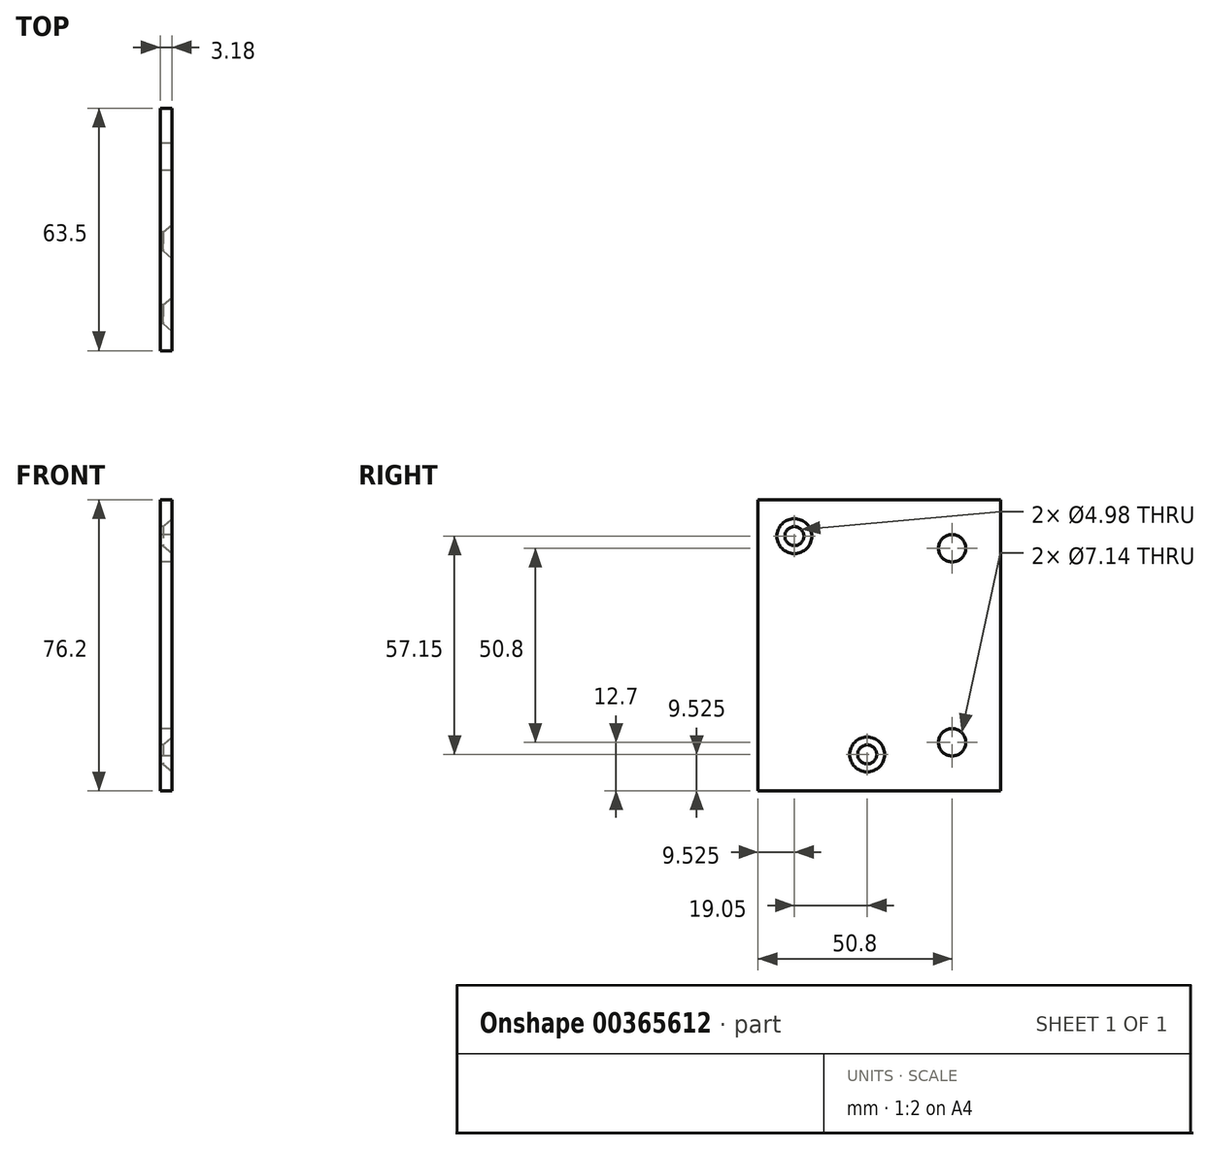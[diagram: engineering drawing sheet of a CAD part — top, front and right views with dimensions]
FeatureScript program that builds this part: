
annotation { "Feature Type Name" : "Feature", "Feature Type Description" : "" }
export const myFeature = defineFeature(function(context is Context, id is Id, definition is map)
    precondition{}
    {
        {
            var Q0;
            Q0=qCreatedBy(makeId("Right.planeOp"),FACE);
            var sketch = newSketch(context, id + "F0", { "sketchPlane" : qUnion([Q0])});
            skLineSegment(sketch, "E0.bottom", {"start": v(31.75, -38.1) * mm, "end": v(-31.75, -38.1) * mm});
            skLineSegment(sketch, "E0.top", {"start": v(31.75, 38.1) * mm, "end": v(-31.75, 38.1) * mm});
            skLineSegment(sketch, "E0.left", {"start": v(31.75, -38.1) * mm, "end": v(31.75, 38.1) * mm});
            skLineSegment(sketch, "E0.right", {"start": v(-31.75, -38.1) * mm, "end": v(-31.75, 38.1) * mm});
            skPoint(sketch, "E0.middle", {"position": v(0, 0) * mm});
            skSolve(sketch);
        }
        {
            var Q0;
            Q0=qSketchRegion(id+"F0",true);
            extrude(context, id + "F1", {"entities" : qUnion([Q0]), "depth" : 3.17 * mm, "offsetDistance" : 25.4 * mm});
        }
        {
            var Q0;
            Q0=makeQuery(id+"F1.opExtrude","CAP_FACE",FACE,{"disambiguationData":[OSD([sQuery(id+"F0.wireOp",EDGE,"E0.bottom"),sQuery(id+"F0.wireOp",EDGE,"E0.top"),sQuery(id+"F0.wireOp",EDGE,"E0.left"),sQuery(id+"F0.wireOp",EDGE,"E0.right")])],"isStart":false});
            var sketch = newSketch(context, id + "F2", { "sketchPlane" : qUnion([Q0])});
            skPoint(sketch, "E1", {"position": v(-22.23, 28.58) * mm});
            skPoint(sketch, "E2", {"position": v(-3.18, -28.58) * mm});
            skSolve(sketch);
        }
        {
            var Q0;
            Q0=sQuery(id+"F2.wireOp",VERTEX,"E1");
            var Q1;
            Q1=sQuery(id+"F2.wireOp",VERTEX,"9c431e09-931f-43e2-840f-4f00e6efbce6");
            var Q2;
            Q2=sQuery(id+"F2.wireOp",VERTEX,"E2");
            var Q3;
            Q3=sQuery(id+"F2.wireOp",VERTEX,"9e30ab42-1027-4ecf-a6f1-ec90ac2d1b19");
            var Q4;
            Q4=makeQuery(id+"F1.opExtrude","SWEPT_BODY",BODY,{"disambiguationData":[OSD([sQuery(id+"F0.wireOp",EDGE,"E0.bottom"),sQuery(id+"F0.wireOp",EDGE,"E0.top"),sQuery(id+"F0.wireOp",EDGE,"E0.left"),sQuery(id+"F0.wireOp",EDGE,"E0.right")])]});
            hole(context, id + "F3", {"style" : HoleStyle.C_SINK, "endStyle" : HoleEndStyle.THROUGH, "standardTappedOrClearance" : lookupTablePath({ "fit" : "Normal (ASME)", "standard" : "ANSI", "size" : "#8", "type" : "Clearance" }), "standardBlindInLast" : lookupTablePath({ "fit" : "Normal", "standard" : "ANSI", "size" : "#8", "type" : "Clearance" }), "holeDiameter" : 4.98 * mm, "cSinkDiameter" : 9.12 * mm, "cSinkAngle" : 82 * degree, "majorDiameter" : 6.35 * mm, "isTappedThrough" : true, "tappedDepth" : 12.7 * mm, "tapClearance" : 3, "locations" : qUnion([Q0, Q1, Q2, Q3]), "scope" : qUnion([Q4]), "startStyle" : HoleStartStyle.SKETCH});
        }
        {
            var Q0;
            Q0=makeQuery(id+"F1.opExtrude","CAP_FACE",FACE,{"disambiguationData":[OSD([sQuery(id+"F0.wireOp",EDGE,"E0.bottom"),sQuery(id+"F0.wireOp",EDGE,"E0.top"),sQuery(id+"F0.wireOp",EDGE,"E0.left"),sQuery(id+"F0.wireOp",EDGE,"E0.right")])],"isStart":false});
            var sketch = newSketch(context, id + "F4", { "sketchPlane" : qUnion([Q0])});
            skPoint(sketch, "E3", {"position": v(19.05, 25.4) * mm});
            skPoint(sketch, "E4", {"position": v(19.05, -25.4) * mm});
            skSolve(sketch);
        }
        {
            var Q0;
            Q0=sQuery(id+"F4.wireOp",VERTEX,"E3");
            var Q1;
            Q1=sQuery(id+"F4.wireOp",VERTEX,"E4");
            var Q2;
            Q2=makeQuery(id+"F1.opExtrude","SWEPT_BODY",BODY,{"disambiguationData":[OSD([sQuery(id+"F0.wireOp",EDGE,"E0.bottom"),sQuery(id+"F0.wireOp",EDGE,"E0.top"),sQuery(id+"F0.wireOp",EDGE,"E0.left"),sQuery(id+"F0.wireOp",EDGE,"E0.right")])]});
            hole(context, id + "F5", {"style" : HoleStyle.SIMPLE, "endStyle" : HoleEndStyle.THROUGH, "standardTappedOrClearance" : lookupTablePath({ "fit" : "Normal (ASME)", "standard" : "ANSI", "size" : "1/4", "type" : "Clearance" }), "standardBlindInLast" : lookupTablePath({ "fit" : "Normal", "standard" : "ANSI", "engagement" : "75%", "pitch" : "20 tpi", "size" : "1/4", "type" : "Clearance & tapped" }), "holeDiameter" : 7.14 * mm, "majorDiameter" : 6.35 * mm, "isTappedThrough" : true, "tappedDepth" : 12.7 * mm, "tapClearance" : 3, "locations" : qUnion([Q0, Q1]), "scope" : qUnion([Q2]), "startStyle" : HoleStartStyle.SKETCH});
        }
    });
